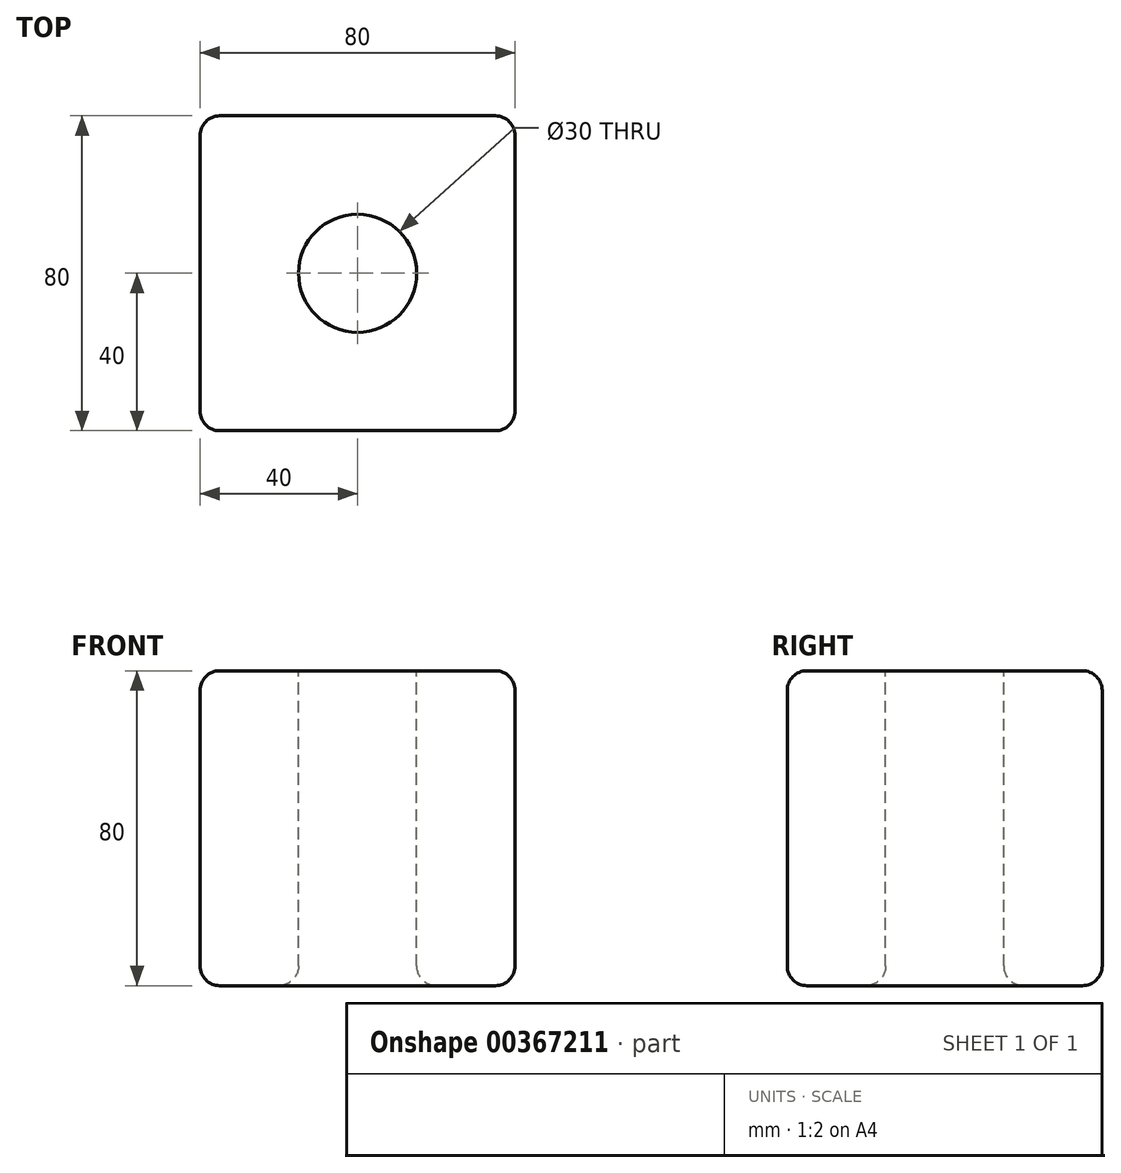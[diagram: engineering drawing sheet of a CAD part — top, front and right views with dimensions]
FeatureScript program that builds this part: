
annotation { "Feature Type Name" : "Feature", "Feature Type Description" : "" }
export const myFeature = defineFeature(function(context is Context, id is Id, definition is map)
    precondition{}
    {
        {
            var Q0;
            Q0=qCreatedBy(makeId("Top.planeOp"),FACE);
            var sketch = newSketch(context, id + "F0", { "sketchPlane" : qUnion([Q0])});
            skLineSegment(sketch, "E0.bottom", {"start": v(40, -40) * mm, "end": v(-40, -40) * mm});
            skLineSegment(sketch, "E0.top", {"start": v(40, 40) * mm, "end": v(-40, 40) * mm});
            skLineSegment(sketch, "E0.left", {"start": v(40, -40) * mm, "end": v(40, 40) * mm});
            skLineSegment(sketch, "E0.right", {"start": v(-40, -40) * mm, "end": v(-40, 40) * mm});
            skPoint(sketch, "E0.middle", {"position": v(0, 0) * mm});
            skSolve(sketch);
        }
        {
            var Q0;
            Q0=makeQuery(id+"F0.imprint","IMPRINT",FACE,{"disambiguationData":[TD([[makeQuery(id+"F0.imprint","IMPRINT",EDGE,{"derivedFrom":sQuery(id+"F0.wireOp",EDGE,"E0.bottom")}),-1.0]])]});
            extrude(context, id + "F1", {"entities" : qUnion([Q0]), "depth" : 80 * mm});
        }
        {
            var Q0;
            Q0=makeQuery(id+"F1.opExtrude","CAP_FACE",FACE,{"disambiguationData":[OSD([sQuery(id+"F0.wireOp",EDGE,"E0.bottom"),sQuery(id+"F0.wireOp",EDGE,"E0.top"),sQuery(id+"F0.wireOp",EDGE,"E0.left"),sQuery(id+"F0.wireOp",EDGE,"E0.right")])],"isStart":false});
            var sketch = newSketch(context, id + "F2", { "sketchPlane" : qUnion([Q0])});
            skCircle(sketch, "E1", {"center": v(0, 0) * mm, "radius": 15 * mm});
            skSolve(sketch);
        }
        {
            var Q0;
            Q0=makeQuery(id+"F2.imprint","IMPRINT",FACE,{"disambiguationData":[TD([[makeQuery(id+"F2.imprint","IMPRINT",EDGE,{"derivedFrom":sQuery(id+"F2.wireOp",EDGE,"E1")}),1.0]])]});
            extrude(context, id + "F3", {"entities" : qUnion([Q0]), "operationType" : NewBodyOperationType.REMOVE, "endBound" : BoundingType.THROUGH_ALL, "oppositeDirection" : true, "depth" : 25 * mm});
        }
        {
            var Q0;
            Q0=makeQuery(id+"F1.opExtrude","CAP_EDGE",EDGE,{"disambiguationData":[OSD([sQuery(id+"F0.wireOp",EDGE,"E0.right")])],"isStart":false});
            var Q1;
            Q1=makeQuery(id+"F1.opExtrude","CAP_EDGE",EDGE,{"disambiguationData":[OSD([sQuery(id+"F0.wireOp",EDGE,"E0.top")])],"isStart":false});
            var Q2;
            Q2=makeQuery(id+"F1.opExtrude","CAP_EDGE",EDGE,{"disambiguationData":[OSD([sQuery(id+"F0.wireOp",EDGE,"E0.left")])],"isStart":false});
            var Q3;
            Q3=makeQuery(id+"F1.opExtrude","CAP_EDGE",EDGE,{"disambiguationData":[OSD([sQuery(id+"F0.wireOp",EDGE,"E0.bottom")])],"isStart":false});
            var Q4;
            Q4=makeQuery(id+"F1.opExtrude","SWEPT_EDGE",EDGE,{"disambiguationData":[OSD([sQuery(id+"F0.wireOp",EDGE,"E0.top"),sQuery(id+"F0.wireOp",EDGE,"E0.left")])]});
            var Q5;
            Q5=makeQuery(id+"F1.opExtrude","CAP_EDGE",EDGE,{"disambiguationData":[OSD([sQuery(id+"F0.wireOp",EDGE,"E0.top")])],"isStart":true});
            var Q6;
            Q6=makeQuery(id+"F1.opExtrude","SWEPT_EDGE",EDGE,{"disambiguationData":[OSD([sQuery(id+"F0.wireOp",EDGE,"E0.top"),sQuery(id+"F0.wireOp",EDGE,"E0.right")])]});
            var Q7;
            Q7=makeQuery(id+"F1.opExtrude","SWEPT_EDGE",EDGE,{"disambiguationData":[OSD([sQuery(id+"F0.wireOp",EDGE,"E0.bottom"),sQuery(id+"F0.wireOp",EDGE,"E0.right")])]});
            var Q8;
            Q8=makeQuery(id+"F1.opExtrude","CAP_EDGE",EDGE,{"disambiguationData":[OSD([sQuery(id+"F0.wireOp",EDGE,"E0.bottom")])],"isStart":true});
            var Q9;
            Q9=makeQuery(id+"F1.opExtrude","CAP_EDGE",EDGE,{"disambiguationData":[OSD([sQuery(id+"F0.wireOp",EDGE,"E0.left")])],"isStart":true});
            var Q10;
            Q10=makeQuery(id+"F1.opExtrude","SWEPT_EDGE",EDGE,{"disambiguationData":[OSD([sQuery(id+"F0.wireOp",EDGE,"E0.bottom"),sQuery(id+"F0.wireOp",EDGE,"E0.left")])]});
            var Q11;
            Q11=makeQuery(id+"F1.opExtrude","CAP_EDGE",EDGE,{"disambiguationData":[OSD([sQuery(id+"F0.wireOp",EDGE,"E0.right")])],"isStart":true});
            var Q12;
            Q12=makeQuery(id+"F3.boolean.opBoolean","COPY",EDGE,{"derivedFrom":makeQuery(id+"F3.opExtrude","CAP_EDGE",EDGE,{"disambiguationData":[OSD([sQuery(id+"F2.wireOp",EDGE,"E1")])],"isStart":true})});
            var Q13;
            Q13=makeQuery(id+"F3.boolean.opBoolean","INTERSECT",EDGE,{"derivedFrom":[makeQuery(id+"F1.opExtrude","CAP_FACE",FACE,{"disambiguationData":[OSD([sQuery(id+"F0.wireOp",EDGE,"E0.bottom"),sQuery(id+"F0.wireOp",EDGE,"E0.top"),sQuery(id+"F0.wireOp",EDGE,"E0.left"),sQuery(id+"F0.wireOp",EDGE,"E0.right")])],"isStart":true}),makeQuery(id+"F3.opExtrude","SWEPT_FACE",FACE,{"disambiguationData":[OSD([sQuery(id+"F2.wireOp",EDGE,"E1")])]})]});
            fillet(context, id + "F4", {"entities" : qUnion([Q0, Q1, Q2, Q3, Q4, Q5, Q6, Q7, Q8, Q9, Q10, Q11, Q12, Q13]), "radius" : 5 * mm, "tangentPropagation" : true, "allowEdgeOverflow" : false});
        }
    });
